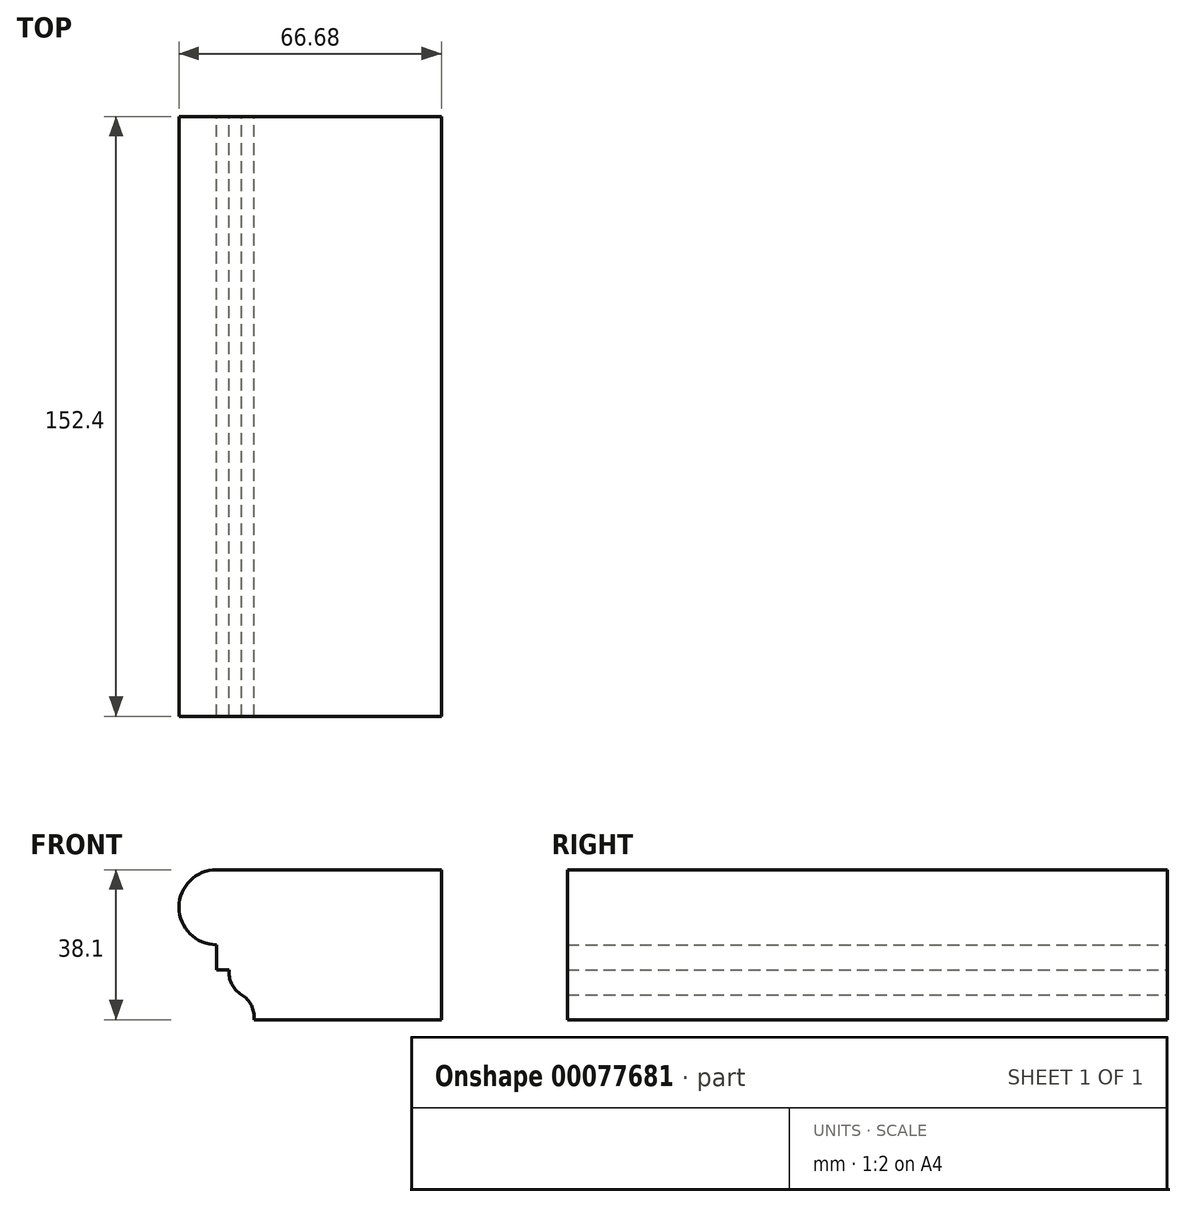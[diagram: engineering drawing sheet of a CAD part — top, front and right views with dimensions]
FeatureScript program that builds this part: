
annotation { "Feature Type Name" : "Feature", "Feature Type Description" : "" }
export const myFeature = defineFeature(function(context is Context, id is Id, definition is map)
    precondition{}
    {
        {
            var Q0;
            Q0=qCreatedBy(makeId("Front.planeOp"),FACE);
            var sketch = newSketch(context, id + "F0", { "sketchPlane" : qUnion([Q0])});
            skLineSegment(sketch, "E0", {"start": v(-4.76, -19.05) * mm, "end": v(-4.76, 19.05) * mm});
            skLineSegment(sketch, "E1", {"start": v(-4.76, 19.05) * mm, "end": v(-23.81, 19.05) * mm});
            skLineSegment(sketch, "E2", {"start": v(-23.81, 0) * mm, "end": v(-23.81, -6.35) * mm});
            skLineSegment(sketch, "E3", {"start": v(-23.81, -6.35) * mm, "end": v(-20.64, -6.35) * mm});
            skLineSegment(sketch, "E4", {"start": v(-4.76, -19.05) * mm, "end": v(-14.29, -19.05) * mm});
            skArc(sketch, "E5", {"start": v(-23.81, 19.05) * mm, "mid": v(-30.55, 16.26) * mm, "end": v(-33.34, 9.53) * mm});
            skArc(sketch, "E6", {"start": v(-33.34, 9.53) * mm, "mid": v(-30.55, 2.79) * mm, "end": v(-23.81, 0) * mm});
            skArc(sketch, "E7", {"start": v(-14.29, -19.05) * mm, "mid": v(-14.95, -15.41) * mm, "end": v(-17.46, -12.7) * mm});
            skArc(sketch, "E8", {"start": v(-20.64, -6.35) * mm, "mid": v(-19.94, -9.97) * mm, "end": v(-17.46, -12.7) * mm});
            skLineSegment(sketch, "E9", {"start": v(33.34, -19.05) * mm, "end": v(-4.76, -19.05) * mm});
            skLineSegment(sketch, "E10", {"start": v(-4.76, 0) * mm, "end": v(33.34, 0) * mm});
            skLineSegment(sketch, "E11", {"start": v(33.34, 0) * mm, "end": v(33.34, -19.05) * mm});
            skLineSegment(sketch, "E12", {"start": v(-4.76, 19.05) * mm, "end": v(33.34, 19.05) * mm});
            skLineSegment(sketch, "E13", {"start": v(33.34, 19.05) * mm, "end": v(33.34, 0) * mm});
            skSolve(sketch);
        }
        {
            var Q0;
            {var subQ0=sQuery(id+"F0.wireOp",EDGE,"E9");Q0=makeQuery(id+"F0.imprint","IMPRINT",FACE,{"disambiguationData":[TD([[makeQuery(id+"F0.imprint","IMPRINT",EDGE,{"derivedFrom":subQ0}),-1.0]])]});}
            var Q1;
            {var subQ0=sQuery(id+"F0.wireOp",EDGE,"E1");Q1=makeQuery(id+"F0.imprint","IMPRINT",FACE,{"disambiguationData":[TD([[makeQuery(id+"F0.imprint","IMPRINT",EDGE,{"derivedFrom":subQ0}),1.0]])]});}
            var Q2;
            {var subQ2=sQuery(id+"F0.wireOp",EDGE,"E10");Q2=makeQuery(id+"F0.imprint","IMPRINT",FACE,{"disambiguationData":[TD([[makeQuery(id+"F0.imprint","IMPRINT",EDGE,{"derivedFrom":subQ2}),1.0]])]});}
            extrude(context, id + "F1", {"entities" : qUnion([Q0, Q1, Q2]), "depth" : 152.4 * mm});
        }
    });
